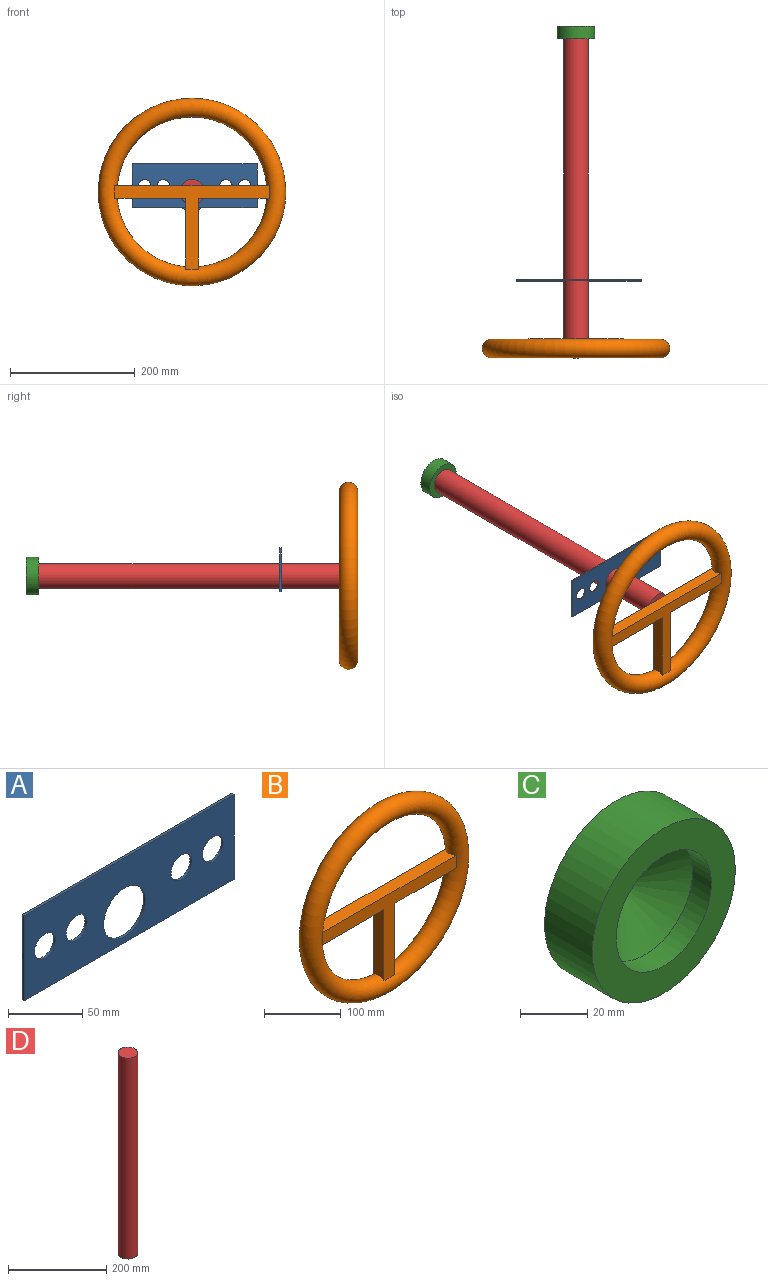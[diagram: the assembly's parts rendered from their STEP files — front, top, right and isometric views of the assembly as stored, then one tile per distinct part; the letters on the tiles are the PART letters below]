
ASSEMBLY  parts=4 mates=3
PART A: 11 faces, bbox 200x2x70 mm
  f0: plane 70x2mm, normal (-1,0,0), area 140mm2, adj f1,f3,f4,f5
  f1: plane 200x2mm, normal (0,0,-1), area 400mm2, adj f0,f2,f4,f5
  f2: plane 70x2mm, normal (1,0,0), area 140mm2, adj f1,f3,f4,f5
  f3: plane 200x2mm, normal (0,0,1), area 400mm2, adj f0,f2,f4,f5
  f4: plane 200x70mm, normal (0,-1,0), area 11486.7mm2, adj f0,f1,f2,f3,f6,f7,f8,f9
  f5: plane 200x70mm, normal (0,1,0), area 11486.7mm2, adj f0,f1,f2,f3,f6,f7,f8,f9
  f6: cylinder r=10mm len=20mm, axis (0,-1,0), area 125.7mm2, adj f4,f5
  f7: cylinder r=10mm len=20mm, axis (0,-1,0), area 125.7mm2, adj f4,f5
  f8: cylinder r=10mm len=20mm, axis (0,-1,0), area 125.7mm2, adj f4,f5
  f9: cylinder r=10mm len=20mm, axis (0,-1,0), area 125.7mm2, adj f4,f5
  f10: cylinder r=20mm len=40mm, axis (0,-1,0), area 251.3mm2, adj f4,f5
PART B: 8 faces, bbox 324.7x20x324.7 mm
  f0: torus R=135mm, axis (0,-1,0), area 78628.6mm2, adj f1,f2,f3,f4,f5,f6,f7
  f1: plane 247.64x133.82mm, normal (0,-1,0), area 7221.1mm2, adj f0,f3,f4,f5,f6,f7
  f2: plane 247.64x133.82mm, normal (0,1,0), area 7221.1mm2, adj f0,f3,f4,f5,f6,f7
  f3: plane 113.42x20.01mm, normal (0,0,-1), area 2215.7mm2, adj f0,f1,f2,f4
  f4: plane 113.42x20.01mm, normal (-1,0,0), area 2215.7mm2, adj f0,f1,f2,f3
  f5: plane 113.42x20.01mm, normal (1,0,0), area 2215.7mm2, adj f0,f1,f2,f6
  f6: plane 113.42x20.01mm, normal (0,0,-1), area 2215.7mm2, adj f0,f1,f2,f5
  f7: plane 246.84x20.01mm, normal (0,0,1), area 4831.7mm2, adj f0,f1,f2
PART C: 5 faces, bbox 60x20x60 mm
  f0: cylinder r=30mm len=60mm, axis (0,1,0), area 3769.9mm2, adj f1,f2
  f1: plane 60x60mm, normal (0,-1,0), area 1570.8mm2, adj f0,f3
  f2: plane 60x60mm, normal (0,1,0), area 2827.4mm2, adj f0
  f3: cylinder r=20mm len=40mm, axis (0,-1,0), area 1000.3mm2, adj f1,f4
  f4: cone r=0mm half-angle=59deg, axis (0,-1,0), area 1466mm2, adj f3
PART D: 3 faces, bbox 40x40x500 mm
  f0: plane 40x40mm, normal (0,0,1), area 1256.6mm2, adj f2
  f1: plane 40x40mm, normal (0,0,-1), area 1256.6mm2, adj f2
  f2: cylinder r=20mm len=500mm, axis (0,0,-1), area 62831.9mm2, adj f0,f1
PLACE A t=(96.41,-93.93,296.22)mm
PLACE B t=(102.83,-188.93,248.94)mm
PLACE C t=(129.72,312.1,226.22)mm
PLACE D rot(axis=(-1,0,0),90deg) t=(106.42,-127.44,228.94)mm
MATE fastened C.f0 <-> D.f2  axis (0,-1,0) through (102.83,306.07,248.94)mm
MATE fastened B.f0 <-> D.f2  axis (0,1,0) through (102.83,-193.93,248.94)mm
MATE slider A.f10 <-> D.f2  axis (0,1,0) through (102.83,-93.93,248.94)mm
